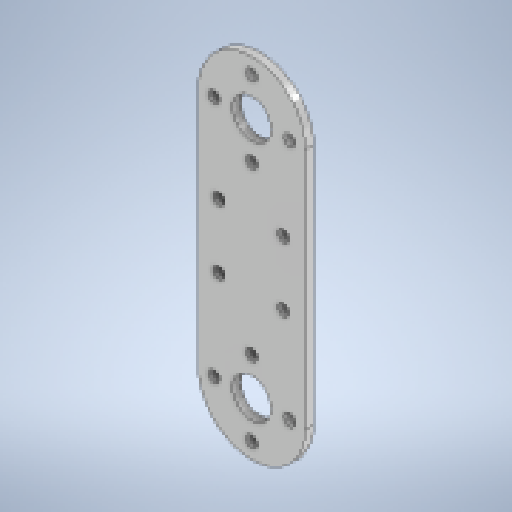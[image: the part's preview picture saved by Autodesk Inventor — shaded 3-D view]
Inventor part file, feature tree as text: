
AUTODESK INVENTOR PART (.ipt)
format: ipt  version: 2024.1 (Build 281209000, 209)  size: 193,024 bytes
history: native  units: in
note: dims shown in document units (in); Inventor stores cm internally (conversion verified against a paired STEP export)
features: reference x9, other x6, sketch x4, hole x2, sheet_metal_op x1, extrude x1
ambient origin geometry x8: Origin, YZ Plane, XZ Plane, XY Plane, X Axis, Y Axis, Z Axis, Center Point
bodies: Solid1 (feature_tree)
feature tree (23):
  sheet_metal_op  "Face1"
  hole  "Hole1"  [1 undecoded]
  extrude  "Extrusion1"  Depth=0.0591in
  hole  "Hole2"  [1 undecoded]
  sketch  "Sketch1"  dims[d0=0.7843in d1=1.7717in]
  other  "Plate1"
  sketch  "Sketch2"  dims[d2=0.0591in]
  reference  "Reference1"
  reference  "Reference2"
  reference  "Reference3"
  reference  "Reference4"
  sketch  "Sketch3"  dims[d3=0.0827in d4=0.2362in d5=0.1575in d6=0.0787in d7=90.0deg d8=0.0591in d9=0.8108in]
  reference  "Reference5"
  sketch  "Sketch4"  dims[d10=0.2835in d11=0.0in d12=0.0in d13=0.0827in d14=0.2362in d15=0.1575in d16=0.0787in d17=90.0deg d18=0.0591in d19=0.8108in]
  reference  "Reference6"
  reference  "Reference7"
  reference  "Reference8"
  reference  "Reference9"
  other  "2_Arm.iam"
  other  "Bottom Horn:1"
  other  "HTD-45H:2"
  other  "HTD-45H:1"
  other  "axis_3_bottom_frame(middle):1"
note: 2 required parameter values undecoded (feature->parameter linkage not recoverable at this tier; creation-order binding heuristic only, values carry confidence <= 0.55)
